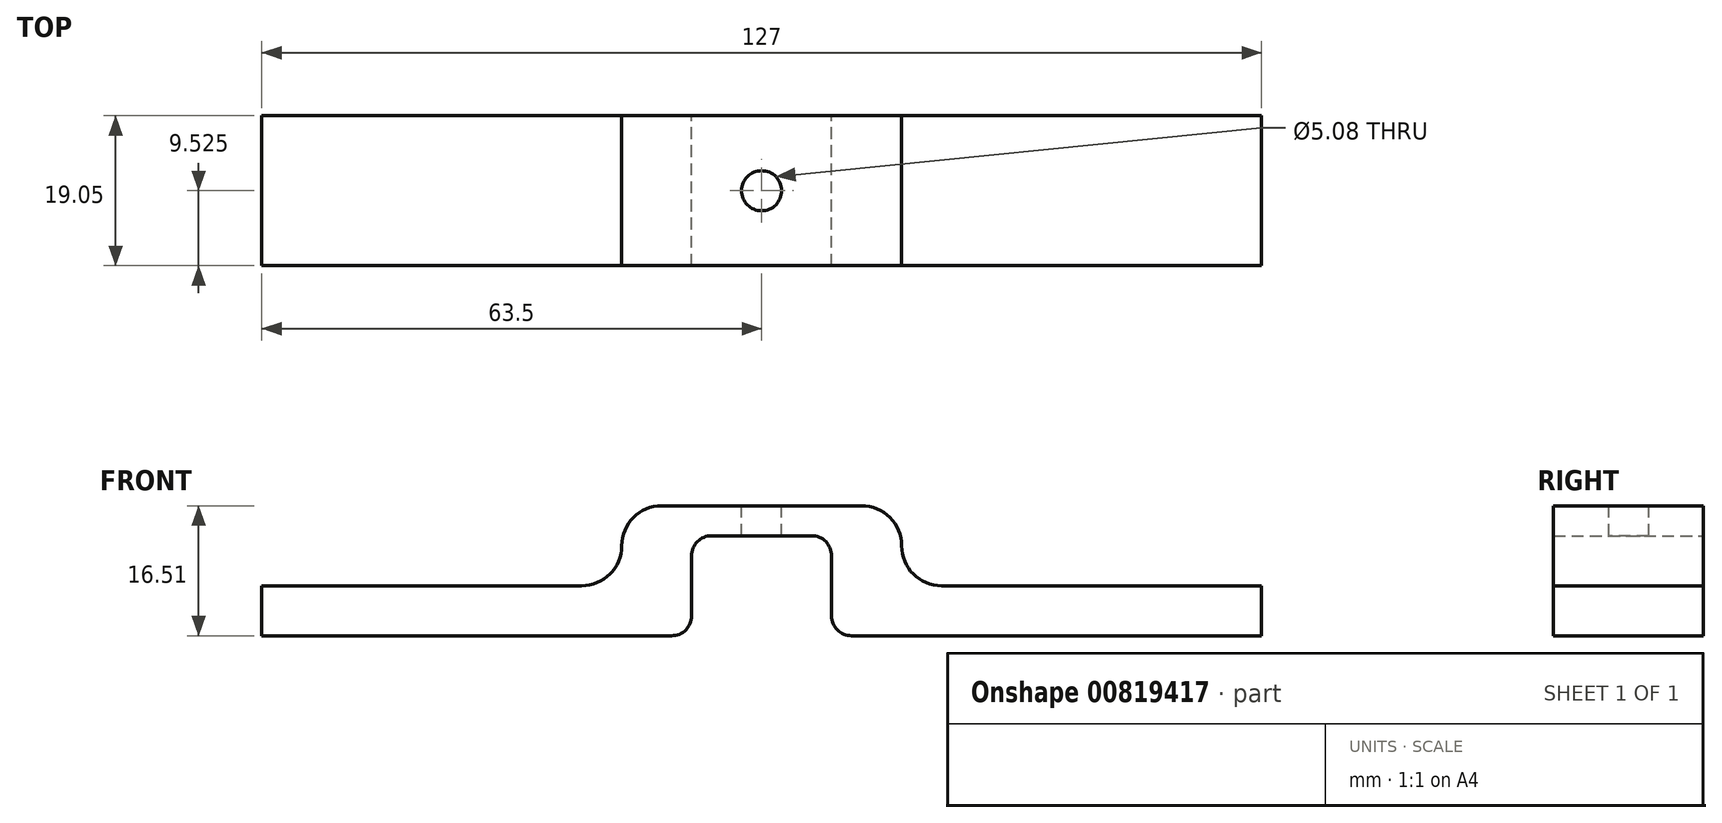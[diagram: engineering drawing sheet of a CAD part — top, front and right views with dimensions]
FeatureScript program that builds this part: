
annotation { "Feature Type Name" : "Feature", "Feature Type Description" : "" }
export const myFeature = defineFeature(function(context is Context, id is Id, definition is map)
    precondition{}
    {
        {
            var Q0;
            Q0=qCreatedBy(makeId("Front.planeOp"),FACE);
            var sketch = newSketch(context, id + "F0", { "sketchPlane" : qUnion([Q0])});
            skLineSegment(sketch, "E0.bottom", {"start": v(63.5, 3.81) * mm, "end": v(-63.5, 3.8) * mm});
            skLineSegment(sketch, "E0.top", {"start": v(63.5, -12.7) * mm, "end": v(-63.5, -12.7) * mm});
            skLineSegment(sketch, "E0.left", {"start": v(63.5, 3.81) * mm, "end": v(63.5, -12.7) * mm});
            skLineSegment(sketch, "E0.right", {"start": v(-63.5, 3.8) * mm, "end": v(-63.5, -12.7) * mm});
            skPoint(sketch, "E0.middle", {"position": v(0, -4.44) * mm});
            skLineSegment(sketch, "E1.bottom", {"start": v(-8.9, 0) * mm, "end": v(8.89, 0) * mm});
            skLineSegment(sketch, "E1.top", {"start": v(-8.9, -12.7) * mm, "end": v(8.89, -12.7) * mm});
            skLineSegment(sketch, "E1.left", {"start": v(-8.9, 0) * mm, "end": v(-8.9, -12.7) * mm});
            skLineSegment(sketch, "E1.right", {"start": v(8.89, 0) * mm, "end": v(8.89, -12.7) * mm});
            skLineSegment(sketch, "E2.bottom", {"start": v(63.5, 3.81) * mm, "end": v(17.78, 3.81) * mm});
            skLineSegment(sketch, "E2.top", {"start": v(63.5, -6.35) * mm, "end": v(17.78, -6.35) * mm});
            skLineSegment(sketch, "E2.left", {"start": v(63.5, 3.81) * mm, "end": v(63.5, -6.35) * mm});
            skLineSegment(sketch, "E2.right", {"start": v(17.78, 3.81) * mm, "end": v(17.78, -6.35) * mm});
            skLineSegment(sketch, "E3.bottom", {"start": v(-63.5, 3.8) * mm, "end": v(-17.78, 3.8) * mm});
            skLineSegment(sketch, "E3.top", {"start": v(-63.5, -6.35) * mm, "end": v(-17.78, -6.35) * mm});
            skLineSegment(sketch, "E3.left", {"start": v(-63.5, 3.8) * mm, "end": v(-63.5, -6.35) * mm});
            skLineSegment(sketch, "E3.right", {"start": v(-17.78, 3.8) * mm, "end": v(-17.78, -6.35) * mm});
            skSolve(sketch);
        }
        {
            var Q0;
            Q0=makeQuery(id+"F0.imprint","IMPRINT",FACE,{"disambiguationData":[TD([[makeQuery(id+"F0.imprint","IMPRINT",EDGE,{"derivedFrom":sQuery(id+"F0.wireOp",EDGE,"E1.bottom")}),1.0]])]});
            extrude(context, id + "F1", {"entities" : qUnion([Q0]), "depth" : 19.05 * mm, "offsetDistance" : 25.4 * mm});
        }
        {
            var Q0;
            Q0=makeQuery(id+"F1.opExtrude","SWEPT_EDGE",EDGE,{"disambiguationData":[OSD([sQuery(id+"F0.wireOp",EDGE,"E0.bottom"),sQuery(id+"F0.wireOp",EDGE,"E2.right")])]});
            var Q1;
            Q1=makeQuery(id+"F1.opExtrude","SWEPT_EDGE",EDGE,{"disambiguationData":[OSD([sQuery(id+"F0.wireOp",EDGE,"E2.top"),sQuery(id+"F0.wireOp",EDGE,"E2.right")])]});
            var Q2;
            Q2=makeQuery(id+"F1.opExtrude","SWEPT_EDGE",EDGE,{"disambiguationData":[OSD([sQuery(id+"F0.wireOp",EDGE,"E0.bottom"),sQuery(id+"F0.wireOp",EDGE,"E3.right")])]});
            var Q3;
            Q3=makeQuery(id+"F1.opExtrude","SWEPT_EDGE",EDGE,{"disambiguationData":[OSD([sQuery(id+"F0.wireOp",EDGE,"E3.top"),sQuery(id+"F0.wireOp",EDGE,"E3.right")])]});
            fillet(context, id + "F2", {"entities" : qUnion([Q0, Q1, Q2, Q3]), "radius" : 5.08 * mm, "tangentPropagation" : true, "allowEdgeOverflow" : false});
        }
        {
            var Q0;
            Q0=makeQuery(id+"F1.opExtrude","SWEPT_FACE",FACE,{"disambiguationData":[OSD([sQuery(id+"F0.wireOp",EDGE,"E0.bottom")])]});
            var sketch = newSketch(context, id + "F3", { "sketchPlane" : qUnion([Q0])});
            skCircle(sketch, "E4", {"center": v(0, -9.53) * mm, "radius": 2.54 * mm});
            skPoint(sketch, "E4.centerSnap0", {"position": v(-12.7, -9.53) * mm});
            skSolve(sketch);
        }
        {
            var Q0;
            Q0=makeQuery(id+"F3.imprint","IMPRINT",FACE,{"disambiguationData":[TD([[makeQuery(id+"F3.imprint","IMPRINT",EDGE,{"derivedFrom":sQuery(id+"F3.wireOp",EDGE,"E4")}),1.0]])]});
            extrude(context, id + "F4", {"entities" : qUnion([Q0]), "operationType" : NewBodyOperationType.REMOVE, "oppositeDirection" : true, "depth" : 25.4 * mm, "offsetDistance" : 25.4 * mm});
        }
        {
            var Q0;
            Q0=makeQuery(id+"F1.opExtrude","SWEPT_EDGE",EDGE,{"disambiguationData":[OSD([sQuery(id+"F0.wireOp",EDGE,"E1.bottom"),sQuery(id+"F0.wireOp",EDGE,"E1.right")])]});
            var Q1;
            Q1=makeQuery(id+"F1.opExtrude","SWEPT_EDGE",EDGE,{"disambiguationData":[OSD([sQuery(id+"F0.wireOp",EDGE,"E1.bottom"),sQuery(id+"F0.wireOp",EDGE,"E1.left")])]});
            var Q2;
            Q2=makeQuery(id+"F1.opExtrude","SWEPT_EDGE",EDGE,{"disambiguationData":[OSD([sQuery(id+"F0.wireOp",EDGE,"E0.top"),sQuery(id+"F0.wireOp",EDGE,"E1.left")])]});
            var Q3;
            Q3=makeQuery(id+"F1.opExtrude","SWEPT_EDGE",EDGE,{"disambiguationData":[OSD([sQuery(id+"F0.wireOp",EDGE,"E0.top"),sQuery(id+"F0.wireOp",EDGE,"E1.right")])]});
            fillet(context, id + "F5", {"entities" : qUnion([Q0, Q1, Q2, Q3]), "radius" : 2.54 * mm, "tangentPropagation" : true, "allowEdgeOverflow" : false});
        }
    });
